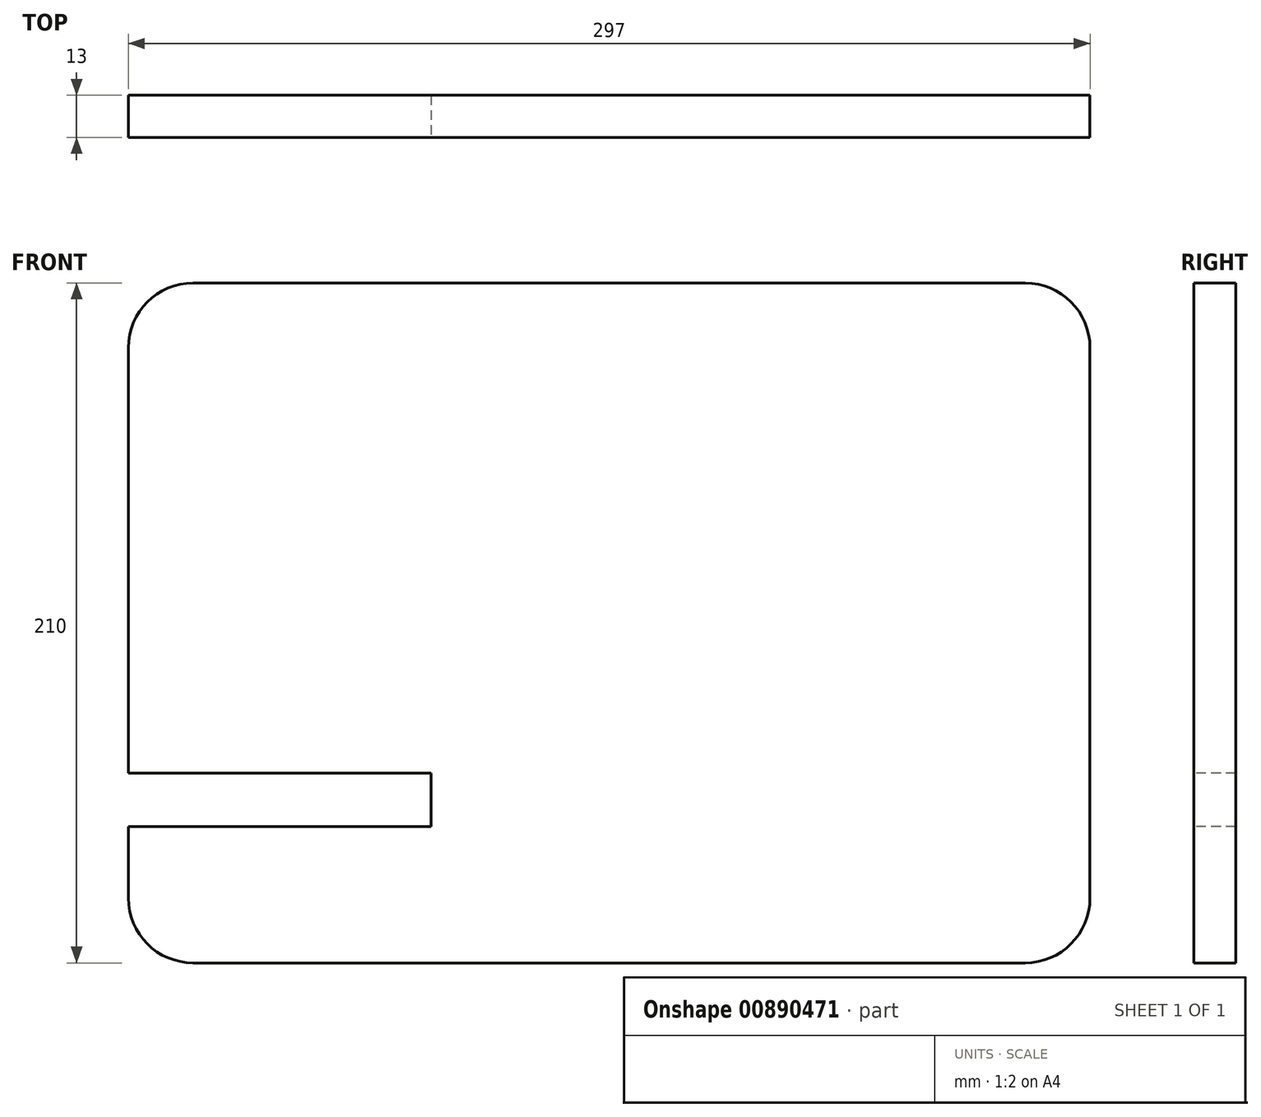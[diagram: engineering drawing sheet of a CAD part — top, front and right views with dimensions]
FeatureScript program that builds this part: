
annotation { "Feature Type Name" : "Feature", "Feature Type Description" : "" }
export const myFeature = defineFeature(function(context is Context, id is Id, definition is map)
    precondition{}
    {
        {
            var Q0;
            Q0=qCreatedBy(makeId("Front.planeOp"),FACE);
            var sketch = newSketch(context, id + "F0", { "sketchPlane" : qUnion([Q0])});
            skLineSegment(sketch, "E0.bottom", {"start": v(-86.2, 86.42) * mm, "end": v(170.8, 86.42) * mm});
            skLineSegment(sketch, "E0.top", {"start": v(-86.2, -123.58) * mm, "end": v(170.8, -123.58) * mm});
            skLineSegment(sketch, "E0.left", {"start": v(-106.2, 66.42) * mm, "end": v(-106.2, -103.58) * mm});
            skLineSegment(sketch, "E0.right", {"start": v(190.8, 66.42) * mm, "end": v(190.8, -103.58) * mm});
            skPoint(sketch, "E1.visualSharp", {"position": v(190.8, -123.58) * mm});
            skArc(sketch, "E1.filletArc", {"start": v(170.8, -123.58) * mm, "mid": v(184.94, -117.72) * mm, "end": v(190.8, -103.58) * mm});
            skPoint(sketch, "E2.visualSharp", {"position": v(-106.2, -123.58) * mm});
            skArc(sketch, "E2.filletArc", {"start": v(-106.2, -103.58) * mm, "mid": v(-100.35, -117.72) * mm, "end": v(-86.2, -123.58) * mm});
            skPoint(sketch, "E3.visualSharp", {"position": v(-106.2, 86.42) * mm});
            skArc(sketch, "E3.filletArc", {"start": v(-86.2, 86.42) * mm, "mid": v(-100.35, 80.56) * mm, "end": v(-106.2, 66.42) * mm});
            skPoint(sketch, "E4.visualSharp", {"position": v(190.8, 86.42) * mm});
            skArc(sketch, "E4.filletArc", {"start": v(190.8, 66.42) * mm, "mid": v(184.94, 80.56) * mm, "end": v(170.8, 86.42) * mm});
            skSolve(sketch);
        }
        {
            var Q0;
            Q0 = qSketchRegion(id + "F0", true);
            extrude(context, id + "F1", {"entities" : qUnion([Q0]), "depth" : 13 * mm, "offsetDistance" : 25 * mm});
        }
        {
            var Q0;
            Q0=makeQuery(id+"F1.opExtrude","CAP_FACE",FACE,{"disambiguationData":[OSD([sQuery(id+"F0.wireOp",EDGE,"E0.bottom"),sQuery(id+"F0.wireOp",EDGE,"E0.top"),sQuery(id+"F0.wireOp",EDGE,"E0.left"),sQuery(id+"F0.wireOp",EDGE,"E0.right"),sQuery(id+"F0.wireOp",EDGE,"E1.filletArc"),sQuery(id+"F0.wireOp",EDGE,"E2.filletArc"),sQuery(id+"F0.wireOp",EDGE,"E3.filletArc"),sQuery(id+"F0.wireOp",EDGE,"E4.filletArc")])],"isStart":false});
            var sketch = newSketch(context, id + "F2", { "sketchPlane" : qUnion([Q0])});
            skLineSegment(sketch, "E5.bottom", {"start": v(-106.2, -64.9) * mm, "end": v(-12.66, -64.9) * mm});
            skLineSegment(sketch, "E5.top", {"start": v(-106.2, -81.5) * mm, "end": v(-12.66, -81.5) * mm});
            skLineSegment(sketch, "E5.left", {"start": v(-106.2, -64.9) * mm, "end": v(-106.2, -81.5) * mm});
            skLineSegment(sketch, "E5.right", {"start": v(-12.66, -64.9) * mm, "end": v(-12.66, -81.5) * mm});
            skSolve(sketch);
        }
        {
            var Q0;
            Q0=makeQuery(id+"F2.imprint","IMPRINT",FACE,{"disambiguationData":[TD([[makeQuery(id+"F2.imprint","IMPRINT",EDGE,{"derivedFrom":sQuery(id+"F2.wireOp",EDGE,"E5.bottom")}),-1.0]])]});
            extrude(context, id + "F3", {"entities" : qUnion([Q0]), "operationType" : NewBodyOperationType.REMOVE, "oppositeDirection" : true, "depth" : 25 * mm, "offsetDistance" : 25 * mm});
        }
    });
